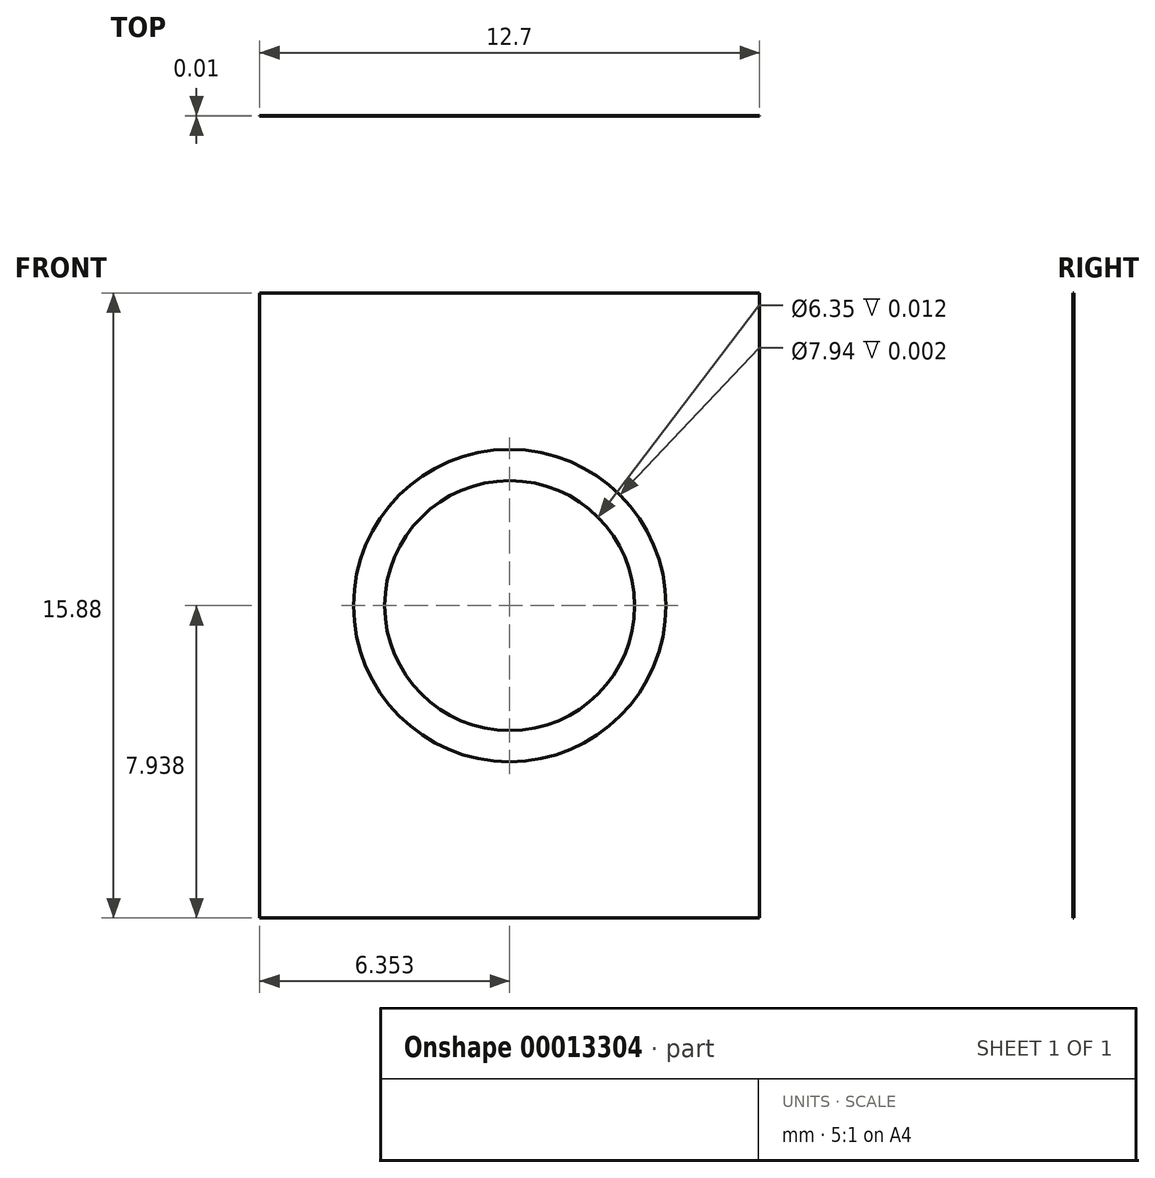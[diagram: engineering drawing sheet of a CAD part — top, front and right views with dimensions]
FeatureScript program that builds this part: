
annotation { "Feature Type Name" : "Feature", "Feature Type Description" : "" }
export const myFeature = defineFeature(function(context is Context, id is Id, definition is map)
    precondition{}
    {
        {
            var Q0;
            Q0=qCreatedBy(makeId("Front.planeOp"),FACE);
            var sketch = newSketch(context, id + "F0", { "sketchPlane" : qUnion([Q0])});
            skLineSegment(sketch, "E0.bottom", {"start": v(-1.02, 3.05) * mm, "end": v(11.68, 3.05) * mm});
            skLineSegment(sketch, "E0.top", {"start": v(-1.02, 18.93) * mm, "end": v(11.68, 18.93) * mm});
            skLineSegment(sketch, "E0.left", {"start": v(-1.02, 3.05) * mm, "end": v(-1.02, 18.93) * mm});
            skLineSegment(sketch, "E0.right", {"start": v(11.68, 3.05) * mm, "end": v(11.68, 18.93) * mm});
            skCircle(sketch, "E1", {"center": v(5.33, 10.99) * mm, "radius": 3.18 * mm});
            skSolve(sketch);
        }
        {
            var Q0;
            Q0 = qSketchRegion(id + "F0", true);
            extrude(context, id + "F1", {"entities" : qUnion([Q0]), "depth" : 3 / 203.2 * mm});
        }
        {
            var Q0;
            Q0=makeQuery(id+"F1.opExtrude","CAP_FACE",FACE,{"disambiguationData":[OSD([sQuery(id+"F0.wireOp",EDGE,"E0.bottom"),sQuery(id+"F0.wireOp",EDGE,"E0.top"),sQuery(id+"F0.wireOp",EDGE,"E0.left"),sQuery(id+"F0.wireOp",EDGE,"E0.right"),sQuery(id+"F0.wireOp",EDGE,"E1")])],"isStart":false});
            var sketch = newSketch(context, id + "F2", { "sketchPlane" : qUnion([Q0])});
            skCircle(sketch, "E2", {"center": v(5.33, 10.99) * mm, "radius": 3.97 * mm});
            skSolve(sketch);
        }
        {
            var Q0;
            Q0 = qSketchRegion(id + "F2", true);
            extrude(context, id + "F3", {"entities" : qUnion([Q0]), "operationType" : NewBodyOperationType.REMOVE, "oppositeDirection" : true, "depth" : 1 / 406.4 * mm});
        }
    });
